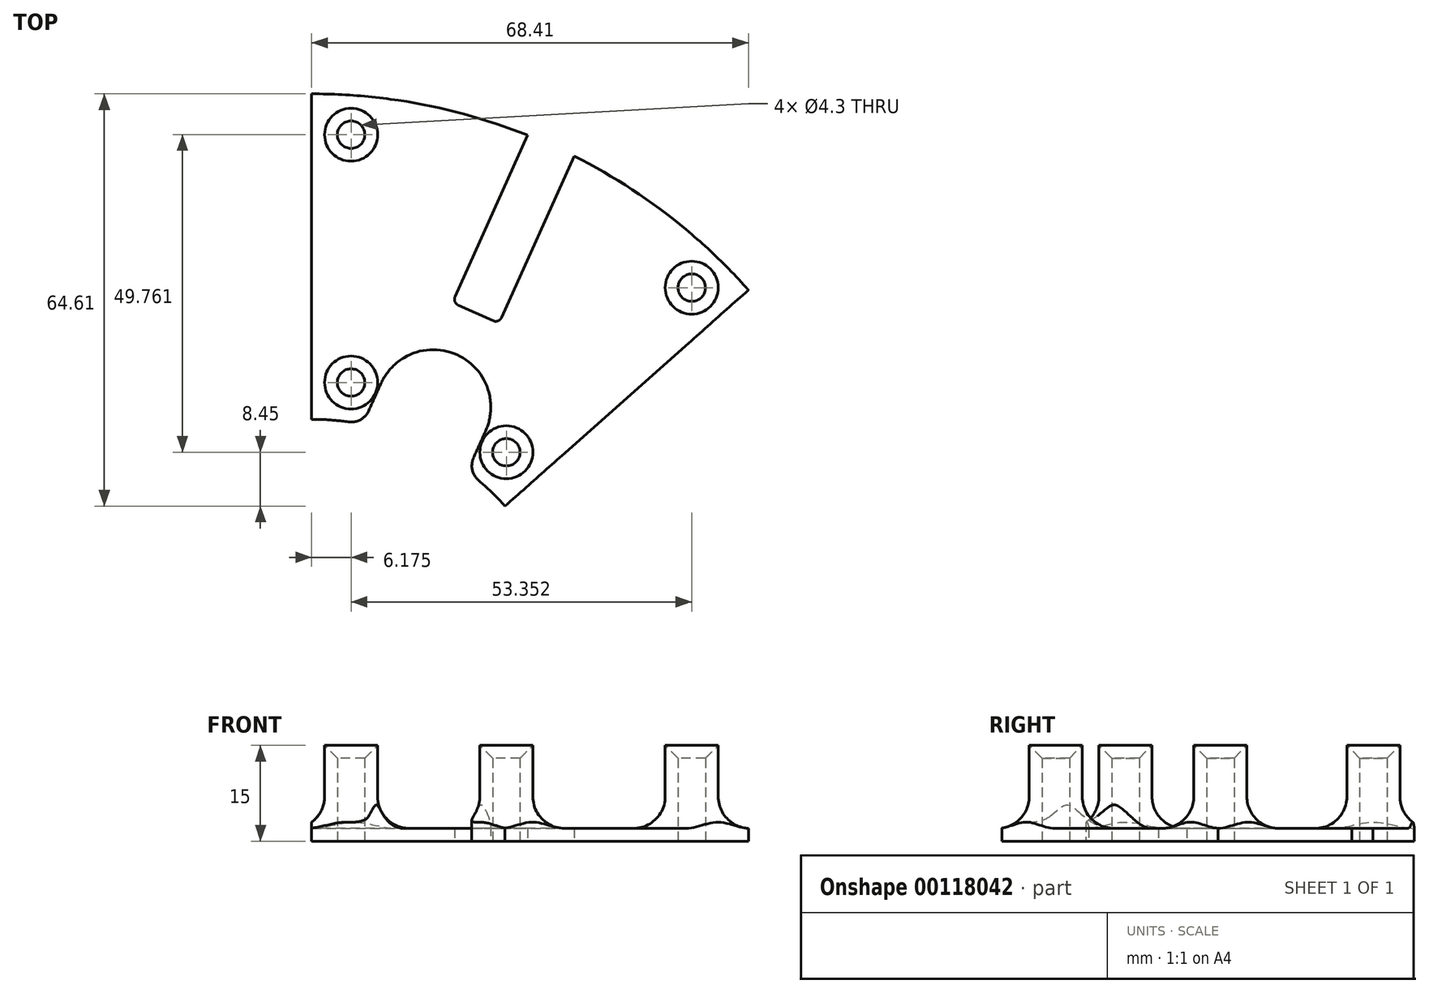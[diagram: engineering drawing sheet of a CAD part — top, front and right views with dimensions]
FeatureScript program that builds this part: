
annotation { "Feature Type Name" : "Feature", "Feature Type Description" : "" }
export const myFeature = defineFeature(function(context is Context, id is Id, definition is map)
    precondition{}
    {
        {
            var Q0;
            Q0=qCreatedBy(makeId("Top.planeOp"),FACE);
            var sketch = newSketch(context, id + "F0", { "sketchPlane" : qUnion([Q0])});
            skArc(sketch, "E0", {"start": v(30.28, 26.9) * mm, "mid": v(28.29, 28.99) * mm, "end": v(26.15, 30.93) * mm});
            skLineSegment(sketch, "E1", {"start": v(0, 40.5) * mm, "end": v(0, 91.5) * mm});
            skLineSegment(sketch, "E2", {"start": v(30.28, 26.9) * mm, "end": v(68.41, 60.76) * mm});
            skArc(sketch, "E3", {"start": v(0, 91.5) * mm, "mid": v(-37.5, -83.46) * mm, "end": v(68.41, 60.76) * mm});
            skArc(sketch, "E4", {"start": v(68.41, 60.76) * mm, "mid": v(55.76, 72.55) * mm, "end": v(41.11, 81.74) * mm});
            skCircle(sketch, "E5", {"center": v(6.17, 85.1) * mm, "radius": 2.15 * mm});
            skCircle(sketch, "E6", {"center": v(59.53, 61.13) * mm, "radius": 2.15 * mm});
            skCircle(sketch, "E7", {"center": v(30.5, 35.34) * mm, "radius": 2.15 * mm});
            skCircle(sketch, "E8", {"center": v(6.17, 46.26) * mm, "radius": 2.15 * mm});
            skLineSegment(sketch, "E9.0", {"start": v(3, 50.93) * mm, "end": v(3, 80.43) * mm});
            skLineSegment(sketch, "E9.2", {"start": v(36.09, 36.07) * mm, "end": v(58.15, 55.66) * mm});
            skArc(sketch, "E9.3", {"start": v(58.23, 66.65) * mm, "mid": v(49.44, 73.4) * mm, "end": v(39.88, 79) * mm});
            skArc(sketch, "E10", {"start": v(4.42, 81.34) * mm, "mid": v(8.96, 82.02) * mm, "end": v(10.1, 86.47) * mm});
            skArc(sketch, "E11", {"start": v(57.95, 64.97) * mm, "mid": v(55.38, 61.17) * mm, "end": v(57.88, 57.32) * mm});
            skArc(sketch, "E12", {"start": v(34.47, 36.53) * mm, "mid": v(30.36, 39.49) * mm, "end": v(26.45, 36.27) * mm});
            skArc(sketch, "E13", {"start": v(9.55, 43.86) * mm, "mid": v(9.37, 48.92) * mm, "end": v(4.42, 50.03) * mm});
            skPoint(sketch, "E14.visualSharp", {"position": v(9.12, 88.03) * mm});
            skArc(sketch, "E14.filletArc", {"start": v(11.16, 87.8) * mm, "mid": v(10.26, 87.43) * mm, "end": v(10.1, 86.47) * mm});
            skPoint(sketch, "E15.visualSharp", {"position": v(3, 82.43) * mm});
            skArc(sketch, "E15.filletArc", {"start": v(4.42, 81.34) * mm, "mid": v(3.46, 81.28) * mm, "end": v(3, 80.43) * mm});
            skPoint(sketch, "E16.visualSharp", {"position": v(3, 48.94) * mm});
            skArc(sketch, "E16.filletArc", {"start": v(3, 50.93) * mm, "mid": v(3.46, 50.09) * mm, "end": v(4.42, 50.03) * mm});
            skPoint(sketch, "E17.visualSharp", {"position": v(8.3, 42.7) * mm});
            skLineSegment(sketch, "E17.filletArc", {"start": v(9.55, 43.86) * mm, "end": v(9.55, 43.86) * mm});
            skPoint(sketch, "E18.visualSharp", {"position": v(26.41, 34.56) * mm});
            skPoint(sketch, "E19.visualSharp", {"position": v(34.6, 34.74) * mm});
            skArc(sketch, "E19.filletArc", {"start": v(34.47, 36.53) * mm, "mid": v(35.15, 35.85) * mm, "end": v(36.09, 36.07) * mm});
            skPoint(sketch, "E20.visualSharp", {"position": v(59.64, 56.98) * mm});
            skArc(sketch, "E20.filletArc", {"start": v(58.15, 55.66) * mm, "mid": v(58.47, 56.56) * mm, "end": v(57.88, 57.32) * mm});
            skPoint(sketch, "E21.visualSharp", {"position": v(59.76, 65.27) * mm});
            skArc(sketch, "E21.filletArc", {"start": v(57.95, 64.97) * mm, "mid": v(58.56, 65.73) * mm, "end": v(58.23, 66.65) * mm});
            skPoint(sketch, "E22.visualSharp", {"position": v(1, 90.5) * mm});
            skPoint(sketch, "E23.visualSharp", {"position": v(1, 41.49) * mm});
            skPoint(sketch, "E24.visualSharp", {"position": v(30.36, 28.3) * mm});
            skPoint(sketch, "E25.visualSharp", {"position": v(67, 60.84) * mm});
            skLineSegment(sketch, "E26.trimOffspring", {"start": v(33.4, 84.1) * mm, "end": v(40.74, 100.44) * mm});
            skLineSegment(sketch, "E27.trimOffspring", {"start": v(40.7, 80.83) * mm, "end": v(48.04, 97.17) * mm});
            skLineSegment(sketch, "E28", {"start": v(16.6, 36.94) * mm, "end": v(17, 37.85) * mm});
            skLineSegment(sketch, "E29.trimOffspring", {"start": v(36.27, 80.73) * mm, "end": v(44.47, 98.98) * mm});
            skPoint(sketch, "E30.start.orphan", {"position": v(15.14, 33.7) * mm});
            skLineSegment(sketch, "E31", {"start": v(36.27, 80.73) * mm, "end": v(23.98, 53.36) * mm});
            skLineSegment(sketch, "E32", {"start": v(22.95, 58.4) * mm, "end": v(28.42, 55.94) * mm});
            skLineSegment(sketch, "E33.trimOffspring", {"start": v(29.75, 56.45) * mm, "end": v(39.88, 79) * mm});
            skLineSegment(sketch, "E34.trimOffspring", {"start": v(22.45, 59.72) * mm, "end": v(32.58, 82.28) * mm});
            skPoint(sketch, "E35.visualSharp", {"position": v(23.94, 43.51) * mm});
            skPoint(sketch, "E36.visualSharp", {"position": v(16.64, 46.8) * mm});
            skPoint(sketch, "E37.visualSharp", {"position": v(29.34, 55.53) * mm});
            skArc(sketch, "E37.filletArc", {"start": v(28.42, 55.94) * mm, "mid": v(29.19, 55.92) * mm, "end": v(29.75, 56.45) * mm});
            skPoint(sketch, "E38.visualSharp", {"position": v(22.04, 58.81) * mm});
            skArc(sketch, "E38.filletArc", {"start": v(22.45, 59.72) * mm, "mid": v(22.43, 58.96) * mm, "end": v(22.95, 58.4) * mm});
            skLineSegment(sketch, "E39", {"start": v(32.58, 82.28) * mm, "end": v(33.4, 84.1) * mm});
            skLineSegment(sketch, "E40", {"start": v(39.88, 79) * mm, "end": v(40.7, 80.83) * mm});
            skArc(sketch, "E41.trimOffspring", {"start": v(33.82, 85.02) * mm, "mid": v(17.22, 89.87) * mm, "end": v(0, 91.5) * mm});
            skArc(sketch, "E42.trimOffspring", {"start": v(32.58, 82.28) * mm, "mid": v(22.05, 85.7) * mm, "end": v(11.16, 87.8) * mm});
            skCircle(sketch, "E43", {"center": v(6.17, 46.26) * mm, "radius": 4.15 * mm});
            skCircle(sketch, "E44", {"center": v(30.5, 35.34) * mm, "radius": 4.15 * mm});
            skCircle(sketch, "E45", {"center": v(59.53, 61.13) * mm, "radius": 4.15 * mm});
            skCircle(sketch, "E46", {"center": v(6.17, 85.1) * mm, "radius": 4.15 * mm});
            skLineSegment(sketch, "E47", {"start": v(20.29, 45.15) * mm, "end": v(15.37, 34.2) * mm});
            skLineSegment(sketch, "E48", {"start": v(25.35, 34.45) * mm, "end": v(27.27, 38.73) * mm});
            skLineSegment(sketch, "E49", {"start": v(8.93, 41.83) * mm, "end": v(10.85, 46.1) * mm});
            skPoint(sketch, "E35.filletArc.end.orphan", {"position": v(23.02, 43.92) * mm});
            skPoint(sketch, "E36.filletArc.start.orphan", {"position": v(17.55, 46.38) * mm});
            skArc(sketch, "E50.trimOffspring", {"start": v(5.76, 40.09) * mm, "mid": v(2.89, 40.4) * mm, "end": v(0, 40.5) * mm});
            skArc(sketch, "E51.trimOffspring", {"start": v(10.06, 42.32) * mm, "mid": v(10.1, 42.31) * mm, "end": v(10.14, 42.3) * mm});
            skArc(sketch, "E52.trimOffspring", {"start": v(27.27, 38.73) * mm, "mid": v(22.75, 50.62) * mm, "end": v(10.85, 46.1) * mm});
            skPoint(sketch, "E53.visualSharp", {"position": v(7.97, 39.7) * mm});
            skArc(sketch, "E53.filletArc", {"start": v(5.76, 40.09) * mm, "mid": v(7.64, 40.43) * mm, "end": v(8.93, 41.83) * mm});
            skPoint(sketch, "E54.visualSharp", {"position": v(24.4, 32.33) * mm});
            skArc(sketch, "E54.filletArc", {"start": v(25.35, 34.45) * mm, "mid": v(25.16, 32.56) * mm, "end": v(26.15, 30.93) * mm});
            skSolve(sketch);
        }
        {
            var Q0;
            Q0=makeQuery(id+"F0.imprint","IMPRINT",FACE,{"disambiguationData":[TD([[makeQuery(id+"F0.imprint","IMPRINT",EDGE,{"derivedFrom":sQuery(id+"F0.wireOp",EDGE,"E1")}),-1.0]])]});
            var Q1;
            Q1=makeQuery(id+"F0.imprint","IMPRINT",FACE,{"disambiguationData":[TD([[makeQuery(id+"F0.imprint","IMPRINT",EDGE,{"derivedFrom":sQuery(id+"F0.wireOp",EDGE,"E5")}),-1.0]])]});
            var Q2;
            Q2=makeQuery(id+"F0.imprint","IMPRINT",FACE,{"disambiguationData":[TD([[makeQuery(id+"F0.imprint","IMPRINT",EDGE,{"derivedFrom":sQuery(id+"F0.wireOp",EDGE,"E8")}),-1.0]])]});
            var Q3;
            Q3=makeQuery(id+"F0.imprint","IMPRINT",FACE,{"disambiguationData":[TD([[makeQuery(id+"F0.imprint","IMPRINT",EDGE,{"derivedFrom":sQuery(id+"F0.wireOp",EDGE,"E7")}),-1.0]])]});
            var Q4;
            {var subQ5=sQuery(id+"F0.wireOp",EDGE,"E0");Q4=makeQuery(id+"F0.imprint","IMPRINT",FACE,{"disambiguationData":[TD([[makeQuery(id+"F0.imprint","IMPRINT",EDGE,{"derivedFrom":subQ5}),-1.0]])]});}
            var Q5;
            Q5=makeQuery(id+"F0.imprint","IMPRINT",FACE,{"disambiguationData":[TD([[makeQuery(id+"F0.imprint","IMPRINT",EDGE,{"derivedFrom":sQuery(id+"F0.wireOp",EDGE,"E6")}),-1.0]])]});
            var Q6;
            Q6=makeQuery(id+"F0.imprint","IMPRINT",FACE,{"disambiguationData":[TD([[makeQuery(id+"F0.imprint","IMPRINT",EDGE,{"derivedFrom":sQuery(id+"F0.wireOp",EDGE,"E9.0")}),-1.0]])]});
            extrude(context, id + "F1", {"entities" : qUnion([Q0, Q1, Q2, Q3, Q4, Q5, Q6]), "depth" : 2 * mm});
        }
        {
            var Q0;
            Q0=qCreatedBy(makeId("Right.planeOp"),FACE);
            var sketch = newSketch(context, id + "F2", { "sketchPlane" : qUnion([Q0])});
            skLineSegment(sketch, "E55", {"start": v(0, 0) * mm, "end": v(97.34, 0) * mm});
            skLineSegment(sketch, "E56", {"start": v(0, 0) * mm, "end": v(0, -30.07) * mm});
            skSolve(sketch);
        }
        {
            var Q0;
            Q0=makeQuery(id+"F0.imprint","IMPRINT",FACE,{"disambiguationData":[TD([[makeQuery(id+"F0.imprint","IMPRINT",EDGE,{"derivedFrom":sQuery(id+"F0.wireOp",EDGE,"E8")}),-1.0]])]});
            var Q1;
            Q1=makeQuery(id+"F0.imprint","IMPRINT",FACE,{"disambiguationData":[TD([[makeQuery(id+"F0.imprint","IMPRINT",EDGE,{"derivedFrom":sQuery(id+"F0.wireOp",EDGE,"E7")}),-1.0]])]});
            var Q2;
            Q2=makeQuery(id+"F0.imprint","IMPRINT",FACE,{"disambiguationData":[TD([[makeQuery(id+"F0.imprint","IMPRINT",EDGE,{"derivedFrom":sQuery(id+"F0.wireOp",EDGE,"E6")}),-1.0]])]});
            var Q3;
            Q3=makeQuery(id+"F0.imprint","IMPRINT",FACE,{"disambiguationData":[TD([[makeQuery(id+"F0.imprint","IMPRINT",EDGE,{"derivedFrom":sQuery(id+"F0.wireOp",EDGE,"E5")}),-1.0]])]});
            extrude(context, id + "F3", {"entities" : qUnion([Q0, Q1, Q2, Q3]), "operationType" : NewBodyOperationType.ADD, "depth" : 15 * mm});
        }
        {
            var Q0;
            Q0=makeQuery(id+"F3.opExtrude","CAP_EDGE",EDGE,{"disambiguationData":[OSD([sQuery(id+"F0.wireOp",EDGE,"E5")])],"isStart":false});
            var Q1;
            Q1=makeQuery(id+"F3.opExtrude","CAP_EDGE",EDGE,{"disambiguationData":[OSD([sQuery(id+"F0.wireOp",EDGE,"E8")])],"isStart":false});
            var Q2;
            Q2=makeQuery(id+"F3.opExtrude","CAP_EDGE",EDGE,{"disambiguationData":[OSD([sQuery(id+"F0.wireOp",EDGE,"E6")])],"isStart":false});
            var Q3;
            Q3=makeQuery(id+"F3.opExtrude","CAP_EDGE",EDGE,{"disambiguationData":[OSD([sQuery(id+"F0.wireOp",EDGE,"E7")])],"isStart":false});
            chamfer(context, id + "F4", {"entities" : qUnion([Q0, Q1, Q2, Q3]), "width" : 2 * mm, "tangentPropagation" : true});
        }
        {
            var Q0;
            Q0=makeQuery(id+"F3.boolean.opBoolean","INTERSECT",EDGE,{"derivedFrom":[makeQuery(id+"F1.opExtrude","CAP_FACE",FACE,{"disambiguationData":[OSD([sQuery(id+"F0.wireOp",EDGE,"E0"),sQuery(id+"F0.wireOp",EDGE,"E1"),sQuery(id+"F0.wireOp",EDGE,"E2"),sQuery(id+"F0.wireOp",EDGE,"E4"),sQuery(id+"F0.wireOp",EDGE,"E5"),sQuery(id+"F0.wireOp",EDGE,"E6"),sQuery(id+"F0.wireOp",EDGE,"E7"),sQuery(id+"F0.wireOp",EDGE,"E8"),sQuery(id+"F0.wireOp",EDGE,"e39d26f6-c48e-407c-a9cd-8ae141cc8811.0"),sQuery(id+"F0.wireOp",EDGE,"bf399b6d-503a-426c-bf46-f8051a25da6f.0"),sQuery(id+"F0.wireOp",EDGE,"E26.trimOffspring"),sQuery(id+"F0.wireOp",EDGE,"E27.trimOffspring"),sQuery(id+"F0.wireOp",EDGE,"fRKwWRrr-ETiV-kwLT-4MPo-dyMSai3vGfdk"),sQuery(id+"F0.wireOp",EDGE,"43f07433-502c-41e9-b1a1-11ddd39e6277.trimOffspring"),sQuery(id+"F0.wireOp",EDGE,"E32"),sQuery(id+"F0.wireOp",EDGE,"E33.trimOffspring"),sQuery(id+"F0.wireOp",EDGE,"E34.trimOffspring"),sQuery(id+"F0.wireOp",EDGE,"E35.filletArc"),sQuery(id+"F0.wireOp",EDGE,"E36.filletArc"),sQuery(id+"F0.wireOp",EDGE,"E37.filletArc"),sQuery(id+"F0.wireOp",EDGE,"E38.filletArc"),sQuery(id+"F0.wireOp",EDGE,"E39"),sQuery(id+"F0.wireOp",EDGE,"E40"),sQuery(id+"F0.wireOp",EDGE,"E41.trimOffspring")])],"isStart":false}),makeQuery(id+"F3.opExtrude","SWEPT_FACE",FACE,{"disambiguationData":[OSD([sQuery(id+"F0.wireOp",EDGE,"E46")])]})]});
            var Q1;
            Q1=makeQuery(id+"F3.boolean.opBoolean","INTERSECT",EDGE,{"derivedFrom":[makeQuery(id+"F1.opExtrude","CAP_FACE",FACE,{"disambiguationData":[OSD([sQuery(id+"F0.wireOp",EDGE,"E0"),sQuery(id+"F0.wireOp",EDGE,"E1"),sQuery(id+"F0.wireOp",EDGE,"E2"),sQuery(id+"F0.wireOp",EDGE,"E4"),sQuery(id+"F0.wireOp",EDGE,"E5"),sQuery(id+"F0.wireOp",EDGE,"E6"),sQuery(id+"F0.wireOp",EDGE,"E7"),sQuery(id+"F0.wireOp",EDGE,"E8"),sQuery(id+"F0.wireOp",EDGE,"e39d26f6-c48e-407c-a9cd-8ae141cc8811.0"),sQuery(id+"F0.wireOp",EDGE,"bf399b6d-503a-426c-bf46-f8051a25da6f.0"),sQuery(id+"F0.wireOp",EDGE,"E26.trimOffspring"),sQuery(id+"F0.wireOp",EDGE,"E27.trimOffspring"),sQuery(id+"F0.wireOp",EDGE,"fRKwWRrr-ETiV-kwLT-4MPo-dyMSai3vGfdk"),sQuery(id+"F0.wireOp",EDGE,"43f07433-502c-41e9-b1a1-11ddd39e6277.trimOffspring"),sQuery(id+"F0.wireOp",EDGE,"E32"),sQuery(id+"F0.wireOp",EDGE,"E33.trimOffspring"),sQuery(id+"F0.wireOp",EDGE,"E34.trimOffspring"),sQuery(id+"F0.wireOp",EDGE,"E35.filletArc"),sQuery(id+"F0.wireOp",EDGE,"E36.filletArc"),sQuery(id+"F0.wireOp",EDGE,"E37.filletArc"),sQuery(id+"F0.wireOp",EDGE,"E38.filletArc"),sQuery(id+"F0.wireOp",EDGE,"E39"),sQuery(id+"F0.wireOp",EDGE,"E40"),sQuery(id+"F0.wireOp",EDGE,"E41.trimOffspring")])],"isStart":false}),makeQuery(id+"F3.opExtrude","SWEPT_FACE",FACE,{"disambiguationData":[OSD([sQuery(id+"F0.wireOp",EDGE,"E43")])]})]});
            var Q2;
            Q2=makeQuery(id+"F3.boolean.opBoolean","INTERSECT",EDGE,{"derivedFrom":[makeQuery(id+"F1.opExtrude","CAP_FACE",FACE,{"disambiguationData":[OSD([sQuery(id+"F0.wireOp",EDGE,"E0"),sQuery(id+"F0.wireOp",EDGE,"E1"),sQuery(id+"F0.wireOp",EDGE,"E2"),sQuery(id+"F0.wireOp",EDGE,"E4"),sQuery(id+"F0.wireOp",EDGE,"E5"),sQuery(id+"F0.wireOp",EDGE,"E6"),sQuery(id+"F0.wireOp",EDGE,"E7"),sQuery(id+"F0.wireOp",EDGE,"E8"),sQuery(id+"F0.wireOp",EDGE,"e39d26f6-c48e-407c-a9cd-8ae141cc8811.0"),sQuery(id+"F0.wireOp",EDGE,"bf399b6d-503a-426c-bf46-f8051a25da6f.0"),sQuery(id+"F0.wireOp",EDGE,"E26.trimOffspring"),sQuery(id+"F0.wireOp",EDGE,"E27.trimOffspring"),sQuery(id+"F0.wireOp",EDGE,"fRKwWRrr-ETiV-kwLT-4MPo-dyMSai3vGfdk"),sQuery(id+"F0.wireOp",EDGE,"43f07433-502c-41e9-b1a1-11ddd39e6277.trimOffspring"),sQuery(id+"F0.wireOp",EDGE,"E32"),sQuery(id+"F0.wireOp",EDGE,"E33.trimOffspring"),sQuery(id+"F0.wireOp",EDGE,"E34.trimOffspring"),sQuery(id+"F0.wireOp",EDGE,"E35.filletArc"),sQuery(id+"F0.wireOp",EDGE,"E36.filletArc"),sQuery(id+"F0.wireOp",EDGE,"E37.filletArc"),sQuery(id+"F0.wireOp",EDGE,"E38.filletArc"),sQuery(id+"F0.wireOp",EDGE,"E39"),sQuery(id+"F0.wireOp",EDGE,"E40"),sQuery(id+"F0.wireOp",EDGE,"E41.trimOffspring")])],"isStart":false}),makeQuery(id+"F3.opExtrude","SWEPT_FACE",FACE,{"disambiguationData":[OSD([sQuery(id+"F0.wireOp",EDGE,"E45")])]})]});
            var Q3;
            Q3=makeQuery(id+"F3.boolean.opBoolean","INTERSECT",EDGE,{"derivedFrom":[makeQuery(id+"F1.opExtrude","CAP_FACE",FACE,{"disambiguationData":[OSD([sQuery(id+"F0.wireOp",EDGE,"E0"),sQuery(id+"F0.wireOp",EDGE,"E1"),sQuery(id+"F0.wireOp",EDGE,"E2"),sQuery(id+"F0.wireOp",EDGE,"E4"),sQuery(id+"F0.wireOp",EDGE,"E5"),sQuery(id+"F0.wireOp",EDGE,"E6"),sQuery(id+"F0.wireOp",EDGE,"E7"),sQuery(id+"F0.wireOp",EDGE,"E8"),sQuery(id+"F0.wireOp",EDGE,"e39d26f6-c48e-407c-a9cd-8ae141cc8811.0"),sQuery(id+"F0.wireOp",EDGE,"bf399b6d-503a-426c-bf46-f8051a25da6f.0"),sQuery(id+"F0.wireOp",EDGE,"E26.trimOffspring"),sQuery(id+"F0.wireOp",EDGE,"E27.trimOffspring"),sQuery(id+"F0.wireOp",EDGE,"fRKwWRrr-ETiV-kwLT-4MPo-dyMSai3vGfdk"),sQuery(id+"F0.wireOp",EDGE,"43f07433-502c-41e9-b1a1-11ddd39e6277.trimOffspring"),sQuery(id+"F0.wireOp",EDGE,"E32"),sQuery(id+"F0.wireOp",EDGE,"E33.trimOffspring"),sQuery(id+"F0.wireOp",EDGE,"E34.trimOffspring"),sQuery(id+"F0.wireOp",EDGE,"E35.filletArc"),sQuery(id+"F0.wireOp",EDGE,"E36.filletArc"),sQuery(id+"F0.wireOp",EDGE,"E37.filletArc"),sQuery(id+"F0.wireOp",EDGE,"E38.filletArc"),sQuery(id+"F0.wireOp",EDGE,"E39"),sQuery(id+"F0.wireOp",EDGE,"E40"),sQuery(id+"F0.wireOp",EDGE,"E41.trimOffspring")])],"isStart":false}),makeQuery(id+"F3.opExtrude","SWEPT_FACE",FACE,{"disambiguationData":[OSD([sQuery(id+"F0.wireOp",EDGE,"E44")])]})]});
            fillet(context, id + "F5", {"entities" : qUnion([Q0, Q1, Q2, Q3]), "radius" : 5 * mm, "tangentPropagation" : true, "allowEdgeOverflow" : false});
        }
    });
